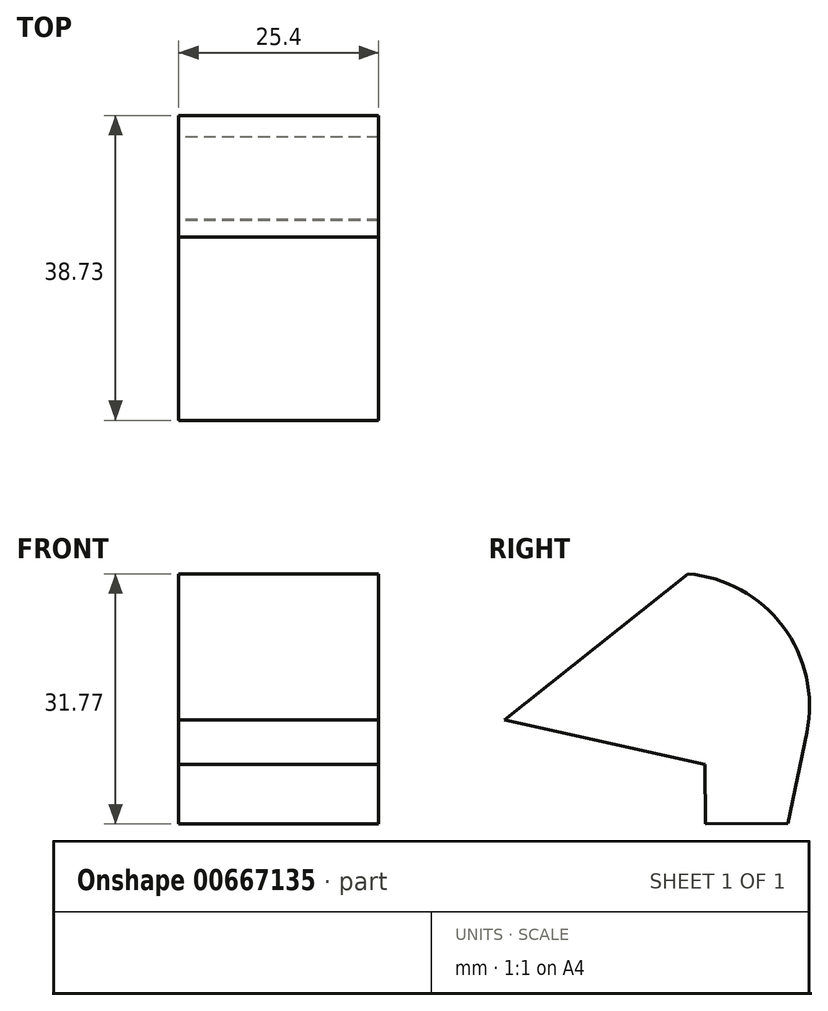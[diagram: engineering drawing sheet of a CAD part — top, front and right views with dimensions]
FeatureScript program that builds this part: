
annotation { "Feature Type Name" : "Feature", "Feature Type Description" : "" }
export const myFeature = defineFeature(function(context is Context, id is Id, definition is map)
    precondition{}
    {
        {
            var Q0;
            Q0=qCreatedBy(makeId("Right.planeOp"),FACE);
            var sketch = newSketch(context, id + "F0", { "sketchPlane" : qUnion([Q0])});
            skLineSegment(sketch, "E0", {"start": v(-52.38, 21.55) * mm, "end": v(-29.1, 40.1) * mm});
            skArc(sketch, "E1", {"start": v(-14, 19.97) * mm, "mid": v(-17, 33.44) * mm, "end": v(-29.1, 40.1) * mm});
            skLineSegment(sketch, "E2", {"start": v(-14, 19.97) * mm, "end": v(-16.38, 8.43) * mm});
            skLineSegment(sketch, "E3", {"start": v(-16.38, 8.43) * mm, "end": v(-26.9, 8.34) * mm});
            skLineSegment(sketch, "E4", {"start": v(-26.9, 8.34) * mm, "end": v(-26.96, 15.9) * mm});
            skLineSegment(sketch, "E5", {"start": v(-26.96, 15.9) * mm, "end": v(-52.38, 21.55) * mm});
            skSolve(sketch);
        }
        {
            var Q0;
            Q0=makeQuery(id+"F0.imprint","IMPRINT",FACE,{"disambiguationData":[TD([[makeQuery(id+"F0.imprint","IMPRINT",EDGE,{"derivedFrom":sQuery(id+"F0.wireOp",EDGE,"E0")}),-1.0]])]});
            extrude(context, id + "F1", {"entities" : qUnion([Q0]), "depth" : 25.4 * mm, "offsetDistance" : 25.4 * mm});
        }
    });
